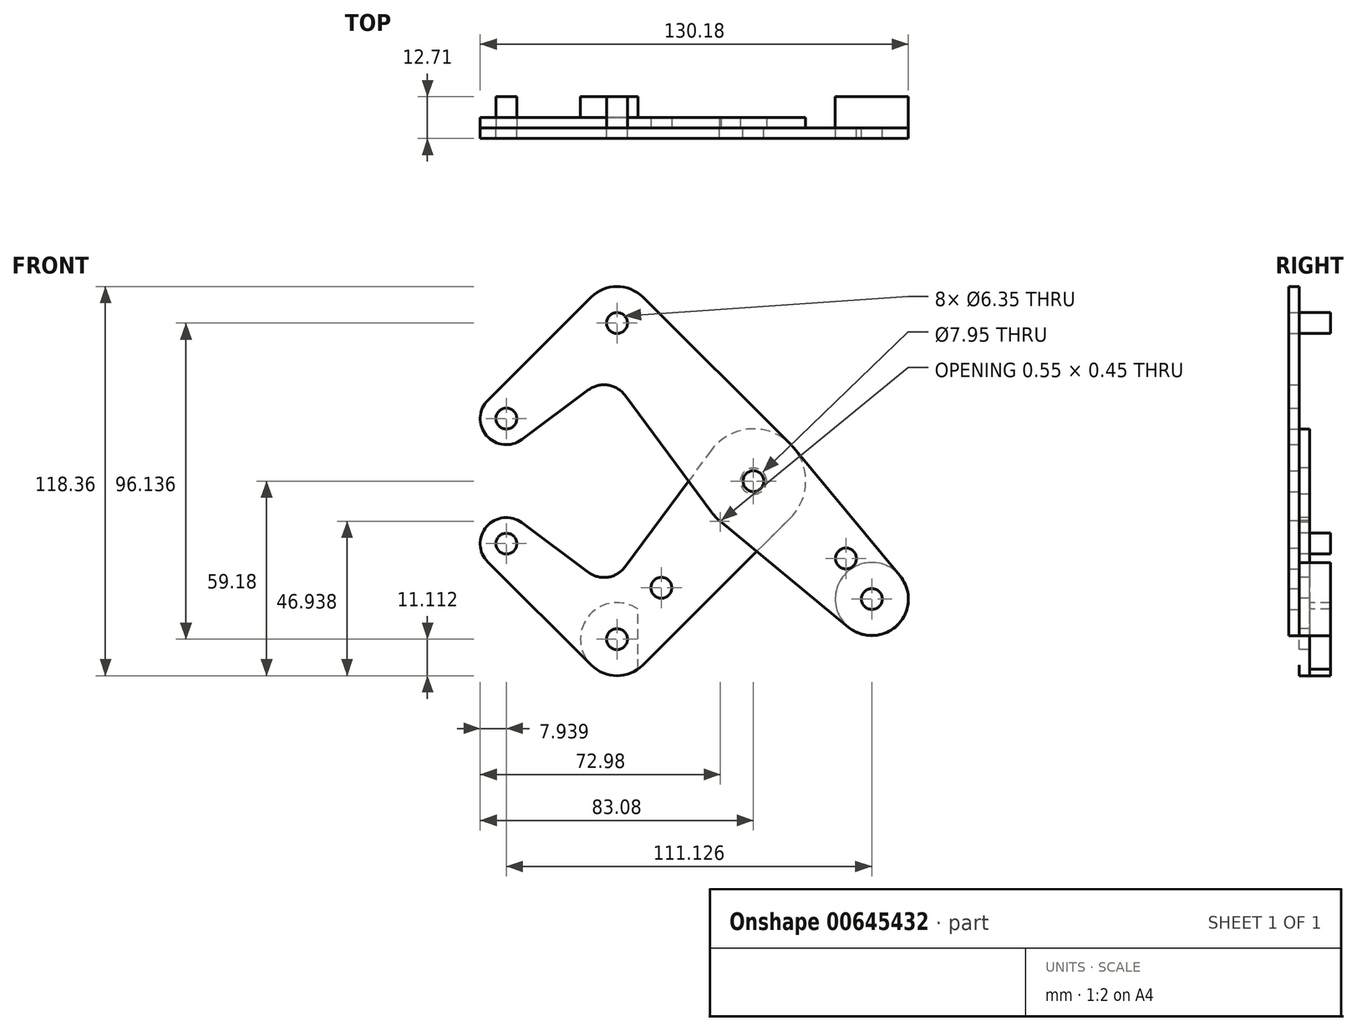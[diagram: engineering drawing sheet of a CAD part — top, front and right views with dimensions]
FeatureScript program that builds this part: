
annotation { "Feature Type Name" : "Feature", "Feature Type Description" : "" }
export const myFeature = defineFeature(function(context is Context, id is Id, definition is map)
    precondition{}
    {
        {
            var Q0;
            Q0=qCreatedBy(makeId("Front.planeOp"),FACE);
            var sketch = newSketch(context, id + "F0", { "sketchPlane" : qUnion([Q0])});
            skLineSegment(sketch, "E0", {"start": v(-41.5, 48.07) * mm, "end": v(0, 0) * mm, "construction": true});
            skLineSegment(sketch, "E1", {"start": v(0, 0) * mm, "end": v(35.99, -35.86) * mm, "construction": true});
            skLineSegment(sketch, "E2", {"start": v(-41.5, 48.07) * mm, "end": v(-75.14, 19.02) * mm, "construction": true});
            skLineSegment(sketch, "E3", {"start": v(0, 0) * mm, "end": v(-41.5, -48.07) * mm, "construction": true});
            skLineSegment(sketch, "E4", {"start": v(-41.5, -48.07) * mm, "end": v(-75.14, -19.02) * mm, "construction": true});
            skCircle(sketch, "E5", {"center": v(0, 0) * mm, "radius": 15.88 * mm});
            skCircle(sketch, "E6", {"center": v(-75.14, 19.02) * mm, "radius": 7.94 * mm});
            skCircle(sketch, "E7", {"center": v(-75.14, -19.02) * mm, "radius": 7.94 * mm});
            skCircle(sketch, "E8", {"center": v(35.99, -35.86) * mm, "radius": 11.11 * mm});
            skCircle(sketch, "E9", {"center": v(35.99, -35.86) * mm, "radius": 3.18 * mm});
            skCircle(sketch, "E10", {"center": v(-75.14, -19.02) * mm, "radius": 3.18 * mm});
            skCircle(sketch, "E11", {"center": v(-75.14, 19.02) * mm, "radius": 3.18 * mm});
            skCircle(sketch, "E12", {"center": v(0, 0) * mm, "radius": 3.98 * mm});
            skCircle(sketch, "E13", {"center": v(0, 0) * mm, "radius": 3.18 * mm});
            skCircle(sketch, "E14", {"center": v(-41.5, 48.07) * mm, "radius": 11.11 * mm});
            skCircle(sketch, "E15", {"center": v(-41.5, -48.07) * mm, "radius": 11.11 * mm});
            skLineSegment(sketch, "E16", {"start": v(-80.74, 24.65) * mm, "end": v(-49.34, 55.94) * mm});
            skLineSegment(sketch, "E17", {"start": v(-80.74, -24.65) * mm, "end": v(-49.34, -55.94) * mm});
            skLineSegment(sketch, "E18", {"start": v(-33.65, -55.94) * mm, "end": v(11.2, -11.25) * mm});
            skLineSegment(sketch, "E19", {"start": v(-33.65, 55.94) * mm, "end": v(11.2, 11.25) * mm});
            skLineSegment(sketch, "E20", {"start": v(12.21, 10.15) * mm, "end": v(44.53, -28.75) * mm});
            skCircle(sketch, "E21", {"center": v(-41.5, 48.07) * mm, "radius": 3.18 * mm});
            skCircle(sketch, "E22", {"center": v(-41.5, -48.07) * mm, "radius": 3.18 * mm});
            skCircle(sketch, "E23", {"center": v(-28, -32.44) * mm, "radius": 3.18 * mm});
            skCircle(sketch, "E24", {"center": v(28.11, -23.53) * mm, "radius": 3.18 * mm});
            skLineSegment(sketch, "E25", {"start": v(28.11, -23.53) * mm, "end": v(25.87, -25.78) * mm, "construction": true});
            skLineSegment(sketch, "E26", {"start": v(-10.37, -12.02) * mm, "end": v(28.91, -44.43) * mm});
            skLineSegment(sketch, "E27", {"start": v(-12.76, -9.44) * mm, "end": v(-39.05, 26.08) * mm});
            skLineSegment(sketch, "E28", {"start": v(-70.4, 12.66) * mm, "end": v(-50.19, 27.72) * mm});
            skLineSegment(sketch, "E29", {"start": v(-70.4, -12.66) * mm, "end": v(-50.19, -27.72) * mm});
            skLineSegment(sketch, "E30", {"start": v(-12.76, 9.44) * mm, "end": v(-39.05, -26.08) * mm});
            skArc(sketch, "E31.filletArc", {"start": v(-39.05, 26.08) * mm, "mid": v(-44.28, 29.22) * mm, "end": v(-50.19, 27.72) * mm});
            skArc(sketch, "E32.filletArc", {"start": v(-50.19, -27.72) * mm, "mid": v(-44.28, -29.22) * mm, "end": v(-39.05, -26.08) * mm});
            skSolve(sketch);
        }
        {
            var Q0;
            Q0=makeQuery(id+"F0.imprint","IMPRINT",FACE,{"disambiguationData":[TD([[makeQuery(id+"F0.imprint","IMPRINT",EDGE,{"derivedFrom":sQuery(id+"F0.wireOp",EDGE,"E11")}),-1.0]])]});
            var Q1;
            {var subQ0=sQuery(id+"F0.wireOp",EDGE,"E16");Q1=makeQuery(id+"F0.imprint","IMPRINT",FACE,{"disambiguationData":[TD([[makeQuery(id+"F0.imprint","IMPRINT",EDGE,{"derivedFrom":subQ0}),-1.0]])]});}
            var Q2;
            Q2=makeQuery(id+"F0.imprint","IMPRINT",FACE,{"disambiguationData":[TD([[makeQuery(id+"F0.imprint","IMPRINT",EDGE,{"derivedFrom":sQuery(id+"F0.wireOp",EDGE,"E21")}),-1.0]])]});
            var Q3;
            Q3=makeQuery(id+"F0.imprint","IMPRINT",FACE,{"disambiguationData":[TD([[makeQuery(id+"F0.imprint","IMPRINT",EDGE,{"derivedFrom":sQuery(id+"F0.wireOp",EDGE,"E12")}),-1.0]])]});
            var Q4;
            {var subQ0=sQuery(id+"F0.wireOp",EDGE,"E27");var subQ1=sQuery(id+"F0.wireOp",EDGE,"E5");var subQ2=makeQuery(id+"F0.imprint","INTERSECT",VERTEX,{"derivedFrom":[subQ1,subQ0]});Q4=makeQuery(id+"F0.imprint","IMPRINT",FACE,{"disambiguationData":[TD([[makeQuery(id+"F0.imprint","IMPRINT",EDGE,{"disambiguationData":[TD([[subQ2,1.0]])],"derivedFrom":subQ1}),-1.0]])]});}
            var Q5;
            {var subQ0=sQuery(id+"F0.wireOp",EDGE,"E18");var subQ1=sQuery(id+"F0.wireOp",EDGE,"E5");var subQ2=makeQuery(id+"F0.imprint","INTERSECT",VERTEX,{"derivedFrom":[subQ1,subQ0]});Q5=makeQuery(id+"F0.imprint","IMPRINT",FACE,{"disambiguationData":[TD([[makeQuery(id+"F0.imprint","IMPRINT",EDGE,{"disambiguationData":[TD([[subQ2,1.0]])],"derivedFrom":subQ1}),-1.0]])]});}
            var Q6;
            {var subQ0=sQuery(id+"F0.wireOp",EDGE,"E20");Q6=makeQuery(id+"F0.imprint","IMPRINT",FACE,{"disambiguationData":[TD([[makeQuery(id+"F0.imprint","IMPRINT",EDGE,{"derivedFrom":subQ0}),-1.0]])]});}
            var Q7;
            Q7=makeQuery(id+"F0.imprint","IMPRINT",FACE,{"disambiguationData":[TD([[makeQuery(id+"F0.imprint","IMPRINT",EDGE,{"derivedFrom":sQuery(id+"F0.wireOp",EDGE,"E9")}),-1.0]])]});
            var Q8;
            Q8=makeQuery(id+"F0.imprint","IMPRINT",FACE,{"disambiguationData":[TD([[makeQuery(id+"F0.imprint","IMPRINT",EDGE,{"derivedFrom":sQuery(id+"F0.wireOp",EDGE,"E12")}),1.0]])]});
            extrude(context, id + "F1", {"entities" : qUnion([Q0, Q1, Q2, Q3, Q4, Q5, Q6, Q7, Q8]), "depth" : 3.17 * mm, "offsetDistance" : 25.4 * mm});
        }
        {
            var Q0;
            Q0=makeQuery(id+"F0.imprint","IMPRINT",FACE,{"disambiguationData":[TD([[makeQuery(id+"F0.imprint","IMPRINT",EDGE,{"derivedFrom":sQuery(id+"F0.wireOp",EDGE,"E12")}),-1.0]])]});
            var Q1;
            {var subQ0=sQuery(id+"F0.wireOp",EDGE,"E18");var subQ1=sQuery(id+"F0.wireOp",EDGE,"E5");var subQ2=makeQuery(id+"F0.imprint","INTERSECT",VERTEX,{"derivedFrom":[subQ1,subQ0]});Q1=makeQuery(id+"F0.imprint","IMPRINT",FACE,{"disambiguationData":[TD([[makeQuery(id+"F0.imprint","IMPRINT",EDGE,{"disambiguationData":[TD([[subQ2,1.0]])],"derivedFrom":subQ1}),-1.0]])]});}
            var Q2;
            {var subQ0=sQuery(id+"F0.wireOp",EDGE,"E27");var subQ1=sQuery(id+"F0.wireOp",EDGE,"E5");var subQ2=makeQuery(id+"F0.imprint","INTERSECT",VERTEX,{"derivedFrom":[subQ1,subQ0]});Q2=makeQuery(id+"F0.imprint","IMPRINT",FACE,{"disambiguationData":[TD([[makeQuery(id+"F0.imprint","IMPRINT",EDGE,{"disambiguationData":[TD([[subQ2,1.0]])],"derivedFrom":subQ1}),-1.0]])]});}
            var Q3;
            {var subQ6=sQuery(id+"F0.wireOp",EDGE,"E17");Q3=makeQuery(id+"F0.imprint","IMPRINT",FACE,{"disambiguationData":[TD([[makeQuery(id+"F0.imprint","IMPRINT",EDGE,{"derivedFrom":subQ6}),1.0]])]});}
            var Q4;
            Q4=makeQuery(id+"F0.imprint","IMPRINT",FACE,{"disambiguationData":[TD([[makeQuery(id+"F0.imprint","IMPRINT",EDGE,{"derivedFrom":sQuery(id+"F0.wireOp",EDGE,"E22")}),-1.0]])]});
            var Q5;
            Q5=makeQuery(id+"F0.imprint","IMPRINT",FACE,{"disambiguationData":[TD([[makeQuery(id+"F0.imprint","IMPRINT",EDGE,{"derivedFrom":sQuery(id+"F0.wireOp",EDGE,"E10")}),-1.0]])]});
            extrude(context, id + "F2", {"entities" : qUnion([Q0, Q1, Q2, Q3, Q4, Q5]), "oppositeDirection" : true, "depth" : 3.17 * mm, "offsetDistance" : 25.4 * mm});
        }
        {
            var Q0;
            Q0=qCreatedBy(makeId("Front.planeOp"),FACE);
            var sketch = newSketch(context, id + "F3", { "sketchPlane" : qUnion([Q0])});
            skPoint(sketch, "E33.0", {"position": v(35.99, -35.86) * mm});
            skPoint(sketch, "E34.0", {"position": v(-41.5, -48.07) * mm});
            skCircle(sketch, "E35.0", {"center": v(-41.5, -48.07) * mm, "radius": 11.11 * mm});
            skLineSegment(sketch, "E36", {"start": v(35.99, -35.86) * mm, "end": v(-35.14, -48.07) * mm, "construction": true});
            skLineSegment(sketch, "E37", {"start": v(-35.14, -38.95) * mm, "end": v(-35.14, -57.19) * mm});
            skCircle(sketch, "E38.0", {"center": v(-75.14, -19.02) * mm, "radius": 3.18 * mm});
            skCircle(sketch, "E39.0", {"center": v(35.99, -35.86) * mm, "radius": 11.11 * mm});
            skCircle(sketch, "E40.0", {"center": v(35.99, -35.86) * mm, "radius": 3.18 * mm});
            skCircle(sketch, "E41.0", {"center": v(-41.5, 48.07) * mm, "radius": 3.18 * mm});
            skSolve(sketch);
        }
        {
            var Q0;
            Q0=qCreatedBy(makeId("Front.planeOp"),FACE);
            cPlane(context, id + "F4", {"entities" : qUnion([Q0]), "cplaneType" : CPlaneType.OFFSET, "offset" : 9.52 * mm, "oppositeDirection" : true, "width" : 152.4 * mm, "height" : 152.4 * mm});
        }
        {
            var Q0;
            {var subQ0=sQuery(id+"F3.wireOp",EDGE,"E37");Q0=makeQuery(id+"F3.imprint","IMPRINT",FACE,{"disambiguationData":[TD([[makeQuery(id+"F3.imprint","IMPRINT",EDGE,{"derivedFrom":subQ0}),-1.0]])]});}
            var Q1;
            Q1=makeQuery(id+"F0.imprint","IMPRINT",FACE,{"disambiguationData":[TD([[makeQuery(id+"F0.imprint","IMPRINT",EDGE,{"derivedFrom":sQuery(id+"F0.wireOp",EDGE,"E9")}),-1.0]])]});
            var Q2;
            Q2=makeQuery(id+"F0.imprint","IMPRINT",FACE,{"disambiguationData":[TD([[makeQuery(id+"F0.imprint","IMPRINT",EDGE,{"derivedFrom":sQuery(id+"F0.wireOp",EDGE,"E9")}),1.0]])]});
            var Q3;
            Q3=makeQuery(id+"F0.imprint","IMPRINT",FACE,{"disambiguationData":[TD([[makeQuery(id+"F0.imprint","IMPRINT",EDGE,{"derivedFrom":sQuery(id+"F0.wireOp",EDGE,"E10")}),1.0]])]});
            var Q4;
            Q4=makeQuery(id+"F0.imprint","IMPRINT",FACE,{"disambiguationData":[TD([[makeQuery(id+"F0.imprint","IMPRINT",EDGE,{"derivedFrom":sQuery(id+"F0.wireOp",EDGE,"E21")}),1.0]])]});
            var Q5;
            Q5=qCreatedBy(id+"F4.planeOp",FACE);
            extrude(context, id + "F5", {"entities" : qUnion([Q0, Q1, Q2, Q3, Q4]), "endBound" : BoundingType.UP_TO_SURFACE, "oppositeDirection" : true, "depth" : 25.4 * mm, "endBoundEntityFace" : qUnion([Q5]), "offsetDistance" : 25.4 * mm});
        }
        {
            var Q0;
            Q0=makeQuery(id+"F1.opExtrude","SWEPT_BODY",BODY,{"disambiguationData":[OSD([sQuery(id+"F0.wireOp",EDGE,"E5"),sQuery(id+"F0.wireOp",EDGE,"E6"),sQuery(id+"F0.wireOp",EDGE,"E8"),sQuery(id+"F0.wireOp",EDGE,"E9"),sQuery(id+"F0.wireOp",EDGE,"E11"),sQuery(id+"F0.wireOp",EDGE,"E13"),sQuery(id+"F0.wireOp",EDGE,"E14"),sQuery(id+"F0.wireOp",EDGE,"E16"),sQuery(id+"F0.wireOp",EDGE,"E19"),sQuery(id+"F0.wireOp",EDGE,"E20"),sQuery(id+"F0.wireOp",EDGE,"E21"),sQuery(id+"F0.wireOp",EDGE,"E24"),sQuery(id+"F0.wireOp",EDGE,"E26"),sQuery(id+"F0.wireOp",EDGE,"E27"),sQuery(id+"F0.wireOp",EDGE,"E28"),sQuery(id+"F0.wireOp",EDGE,"E31.filletArc")])]});
            var Q1;
            Q1=makeQuery(id+"F2.opExtrude","SWEPT_BODY",BODY,{"disambiguationData":[OSD([sQuery(id+"F0.wireOp",EDGE,"E5"),sQuery(id+"F0.wireOp",EDGE,"E7"),sQuery(id+"F0.wireOp",EDGE,"E10"),sQuery(id+"F0.wireOp",EDGE,"E12"),sQuery(id+"F0.wireOp",EDGE,"E15"),sQuery(id+"F0.wireOp",EDGE,"E17"),sQuery(id+"F0.wireOp",EDGE,"E18"),sQuery(id+"F0.wireOp",EDGE,"E22"),sQuery(id+"F0.wireOp",EDGE,"E23"),sQuery(id+"F0.wireOp",EDGE,"E26"),sQuery(id+"F0.wireOp",EDGE,"E29"),sQuery(id+"F0.wireOp",EDGE,"E30"),sQuery(id+"F0.wireOp",EDGE,"E32.filletArc")])]});
            var Q2;
            Q2=makeQuery(id+"F5.opExtrude","SWEPT_BODY",BODY,{"disambiguationData":[OSD([sQuery(id+"F0.wireOp",EDGE,"E8")])]});
            var Q3;
            Q3=makeQuery(id+"F5.opExtrude","SWEPT_BODY",BODY,{"disambiguationData":[OSD([sQuery(id+"F3.wireOp",EDGE,"E35.0"),sQuery(id+"F3.wireOp",EDGE,"E37")])]});
            var Q4;
            Q4=makeQuery(id+"F5.opExtrude","SWEPT_BODY",BODY,{"disambiguationData":[OSD([sQuery(id+"F0.wireOp",EDGE,"E21")])]});
            var Q5;
            Q5=makeQuery(id+"F5.opExtrude","SWEPT_BODY",BODY,{"disambiguationData":[OSD([sQuery(id+"F0.wireOp",EDGE,"E10")])]});
            booleanBodies(context, id + "F6", {"operationType" : BooleanOperationType.SUBTRACTION, "tools" : qUnion([Q0, Q1]), "targets" : qUnion([Q2, Q3, Q4, Q5]), "keepTools" : true});
        }
    });
